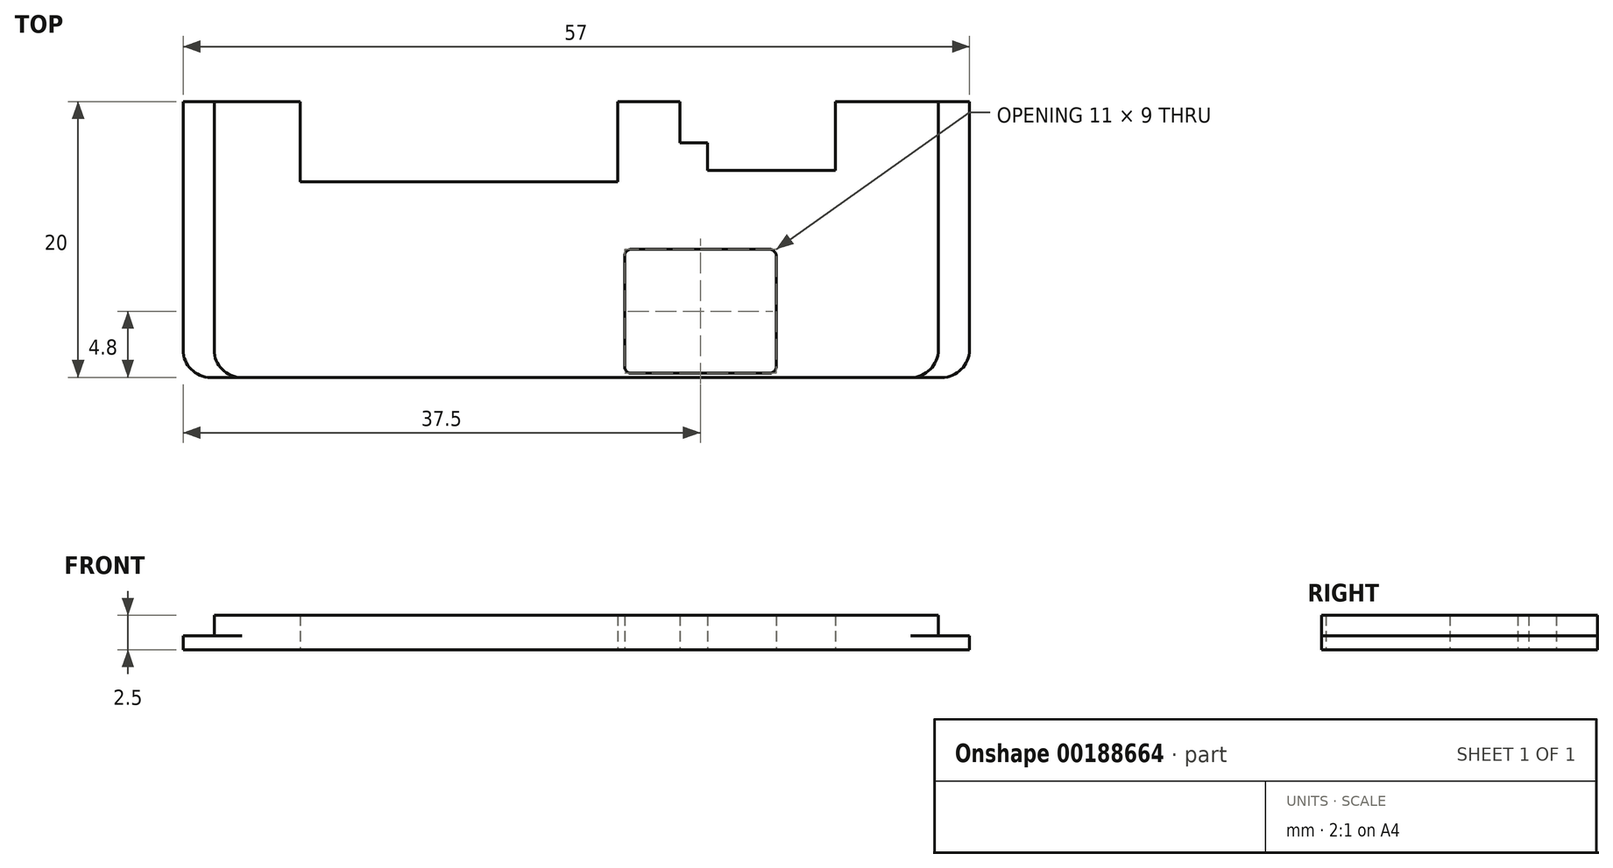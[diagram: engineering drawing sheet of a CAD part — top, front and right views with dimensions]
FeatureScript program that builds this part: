
annotation { "Feature Type Name" : "Feature", "Feature Type Description" : "" }
export const myFeature = defineFeature(function(context is Context, id is Id, definition is map)
    precondition{}
    {
        {
            var Q0;
            Q0=qCreatedBy(makeId("Top.planeOp"),FACE);
            var sketch = newSketch(context, id + "F0", { "sketchPlane" : qUnion([Q0])});
            skLineSegment(sketch, "E0.bottom", {"start": v(2, 0) * mm, "end": v(55, 0) * mm});
            skLineSegment(sketch, "E0.top", {"start": v(0, 20) * mm, "end": v(57, 20) * mm});
            skLineSegment(sketch, "E0.left", {"start": v(0, 2) * mm, "end": v(0, 20) * mm});
            skLineSegment(sketch, "E0.right", {"start": v(57, 2) * mm, "end": v(57, 20) * mm});
            skPoint(sketch, "E1.visualSharp", {"position": v(0, 0) * mm});
            skArc(sketch, "E1.filletArc", {"start": v(0, 2) * mm, "mid": v(0.59, 0.59) * mm, "end": v(2, 0) * mm});
            skPoint(sketch, "E2.visualSharp", {"position": v(57, 0) * mm});
            skArc(sketch, "E2.filletArc", {"start": v(55, 0) * mm, "mid": v(56.41, 0.59) * mm, "end": v(57, 2) * mm});
            skSolve(sketch);
        }
        {
            var Q0;
            Q0=qSketchRegion(id+"F0",true);
            extrude(context, id + "F1", {"entities" : qUnion([Q0]), "depth" : 1 * mm});
        }
        {
            var Q0;
            Q0=makeQuery(id+"F1.opExtrude","CAP_FACE",FACE,{"disambiguationData":[OSD([sQuery(id+"F0.wireOp",EDGE,"E0.bottom"),sQuery(id+"F0.wireOp",EDGE,"E0.top"),sQuery(id+"F0.wireOp",EDGE,"E0.left"),sQuery(id+"F0.wireOp",EDGE,"E0.right")])],"isStart":false});
            var sketch = newSketch(context, id + "F2", { "sketchPlane" : qUnion([Q0])});
            skLineSegment(sketch, "E3", {"start": v(2.25, 20) * mm, "end": v(54.75, 20) * mm});
            skLineSegment(sketch, "E4", {"start": v(54.75, 20) * mm, "end": v(54.75, 2) * mm});
            skLineSegment(sketch, "E5", {"start": v(52.75, 0) * mm, "end": v(4.25, 0) * mm});
            skLineSegment(sketch, "E6", {"start": v(2.25, 2) * mm, "end": v(2.25, 20) * mm});
            skPoint(sketch, "E7", {"position": v(28.5, 20) * mm});
            skPoint(sketch, "E8.visualSharp", {"position": v(2.25, 0) * mm});
            skArc(sketch, "E8.filletArc", {"start": v(2.25, 2) * mm, "mid": v(2.84, 0.59) * mm, "end": v(4.25, 0) * mm});
            skPoint(sketch, "E9.visualSharp", {"position": v(54.75, 0) * mm});
            skArc(sketch, "E9.filletArc", {"start": v(52.75, 0) * mm, "mid": v(54.16, 0.59) * mm, "end": v(54.75, 2) * mm});
            skSolve(sketch);
        }
        {
            var Q0;
            Q0=qSketchRegion(id+"F2",true);
            extrude(context, id + "F3", {"entities" : qUnion([Q0]), "operationType" : NewBodyOperationType.ADD, "depth" : 1.5 * mm});
        }
        {
            var Q0;
            Q0=makeQuery(id+"F0.imprint","IMPRINT",FACE,{"disambiguationData":[TD([[makeQuery(id+"F0.imprint","IMPRINT",EDGE,{"derivedFrom":sQuery(id+"F0.wireOp",EDGE,"E0.bottom")}),1.0]])]});
            var sketch = newSketch(context, id + "F4", { "sketchPlane" : qUnion([Q0])});
            skLineSegment(sketch, "E10.bottom", {"start": v(41.75, 6.35) * mm, "end": v(33.25, 6.35) * mm, "construction": true});
            skLineSegment(sketch, "E10.top", {"start": v(41.75, 3.25) * mm, "end": v(33.25, 3.25) * mm, "construction": true});
            skLineSegment(sketch, "E10.left", {"start": v(41.75, 6.35) * mm, "end": v(41.75, 3.25) * mm, "construction": true});
            skLineSegment(sketch, "E10.right", {"start": v(33.25, 6.35) * mm, "end": v(33.25, 3.25) * mm, "construction": true});
            skLineSegment(sketch, "E11.bottom", {"start": v(31.5, 20) * mm, "end": v(8.5, 20) * mm});
            skLineSegment(sketch, "E11.top", {"start": v(31.5, 14.2) * mm, "end": v(8.5, 14.2) * mm});
            skLineSegment(sketch, "E11.left", {"start": v(31.5, 20) * mm, "end": v(31.5, 14.2) * mm});
            skLineSegment(sketch, "E11.right", {"start": v(8.5, 20) * mm, "end": v(8.5, 14.2) * mm});
            skLineSegment(sketch, "E12.bottom", {"start": v(36, 20) * mm, "end": v(47.3, 20) * mm});
            skLineSegment(sketch, "E12.top", {"start": v(38, 15) * mm, "end": v(47.3, 15) * mm});
            skLineSegment(sketch, "E12.right", {"start": v(47.3, 20) * mm, "end": v(47.3, 15) * mm});
            skPoint(sketch, "E13", {"position": v(37.5, 3.25) * mm});
            skLineSegment(sketch, "E14", {"start": v(38, 15) * mm, "end": v(38, 17) * mm});
            skLineSegment(sketch, "E15", {"start": v(36, 17) * mm, "end": v(38, 17) * mm});
            skLineSegment(sketch, "E16", {"start": v(36, 17) * mm, "end": v(36, 20) * mm});
            skLineSegment(sketch, "E17.bottom", {"start": v(32.5, 9.3) * mm, "end": v(42.5, 9.3) * mm});
            skLineSegment(sketch, "E17.top", {"start": v(32.5, 0.3) * mm, "end": v(42.5, 0.3) * mm});
            skLineSegment(sketch, "E17.left", {"start": v(32, 8.8) * mm, "end": v(32, 0.8) * mm});
            skLineSegment(sketch, "E17.right", {"start": v(43, 8.8) * mm, "end": v(43, 0.8) * mm});
            skPoint(sketch, "E18", {"position": v(37.5, 9.3) * mm});
            skPoint(sketch, "E19", {"position": v(32, 4.8) * mm});
            skPoint(sketch, "E20", {"position": v(33.25, 4.8) * mm});
            skPoint(sketch, "E21.visualSharp", {"position": v(32, 9.3) * mm});
            skArc(sketch, "E21.filletArc", {"start": v(32.5, 9.3) * mm, "mid": v(32.15, 9.15) * mm, "end": v(32, 8.8) * mm});
            skPoint(sketch, "E22.visualSharp", {"position": v(43, 9.3) * mm});
            skArc(sketch, "E22.filletArc", {"start": v(43, 8.8) * mm, "mid": v(42.85, 9.15) * mm, "end": v(42.5, 9.3) * mm});
            skPoint(sketch, "E23.visualSharp", {"position": v(43, 0.3) * mm});
            skArc(sketch, "E23.filletArc", {"start": v(42.5, 0.3) * mm, "mid": v(42.85, 0.45) * mm, "end": v(43, 0.8) * mm});
            skPoint(sketch, "E24.visualSharp", {"position": v(32, 0.3) * mm});
            skArc(sketch, "E24.filletArc", {"start": v(32, 0.8) * mm, "mid": v(32.15, 0.45) * mm, "end": v(32.5, 0.3) * mm});
            skSolve(sketch);
        }
        {
            var Q0;
            Q0=qSketchRegion(id+"F4",true);
            extrude(context, id + "F5", {"entities" : qUnion([Q0]), "operationType" : NewBodyOperationType.REMOVE, "endBound" : BoundingType.UP_TO_NEXT, "depth" : 25 * mm});
        }
    });
